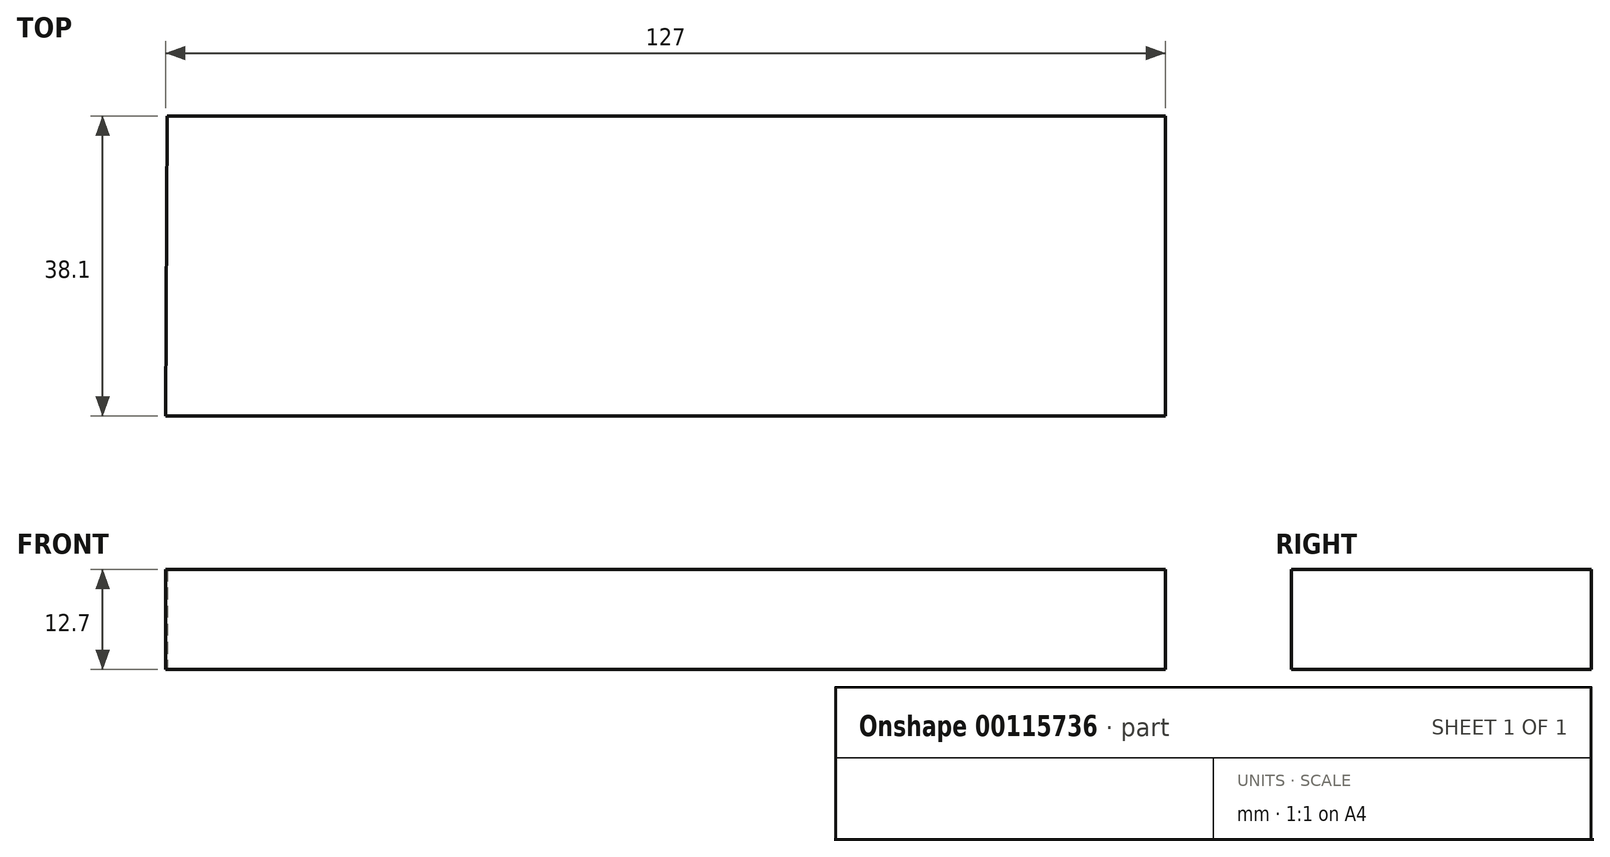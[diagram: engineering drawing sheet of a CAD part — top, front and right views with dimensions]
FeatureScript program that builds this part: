
annotation { "Feature Type Name" : "Feature", "Feature Type Description" : "" }
export const myFeature = defineFeature(function(context is Context, id is Id, definition is map)
    precondition{}
    {
        {
            var Q0;
            Q0=qCreatedBy(makeId("Top.planeOp"),FACE);
            var sketch = newSketch(context, id + "F0", { "sketchPlane" : qUnion([Q0])});
            skLineSegment(sketch, "E0", {"start": v(-76.16, 0) * mm, "end": v(50.66, 0) * mm});
            skLineSegment(sketch, "E1", {"start": v(50.66, 0) * mm, "end": v(50.66, -38.1) * mm});
            skLineSegment(sketch, "E2", {"start": v(50.66, -38.1) * mm, "end": v(-76.34, -38.1) * mm});
            skLineSegment(sketch, "E3", {"start": v(-76.34, -38.1) * mm, "end": v(-76.16, 0) * mm});
            skSolve(sketch);
        }
        {
            var Q0;
            Q0=makeQuery(id+"F0.imprint","IMPRINT",FACE,{"disambiguationData":[TD([[makeQuery(id+"F0.imprint","IMPRINT",EDGE,{"derivedFrom":sQuery(id+"F0.wireOp",EDGE,"E0")}),-1.0]])]});
            extrude(context, id + "F1", {"entities" : qUnion([Q0]), "depth" : 12.7 * mm});
        }
    });
